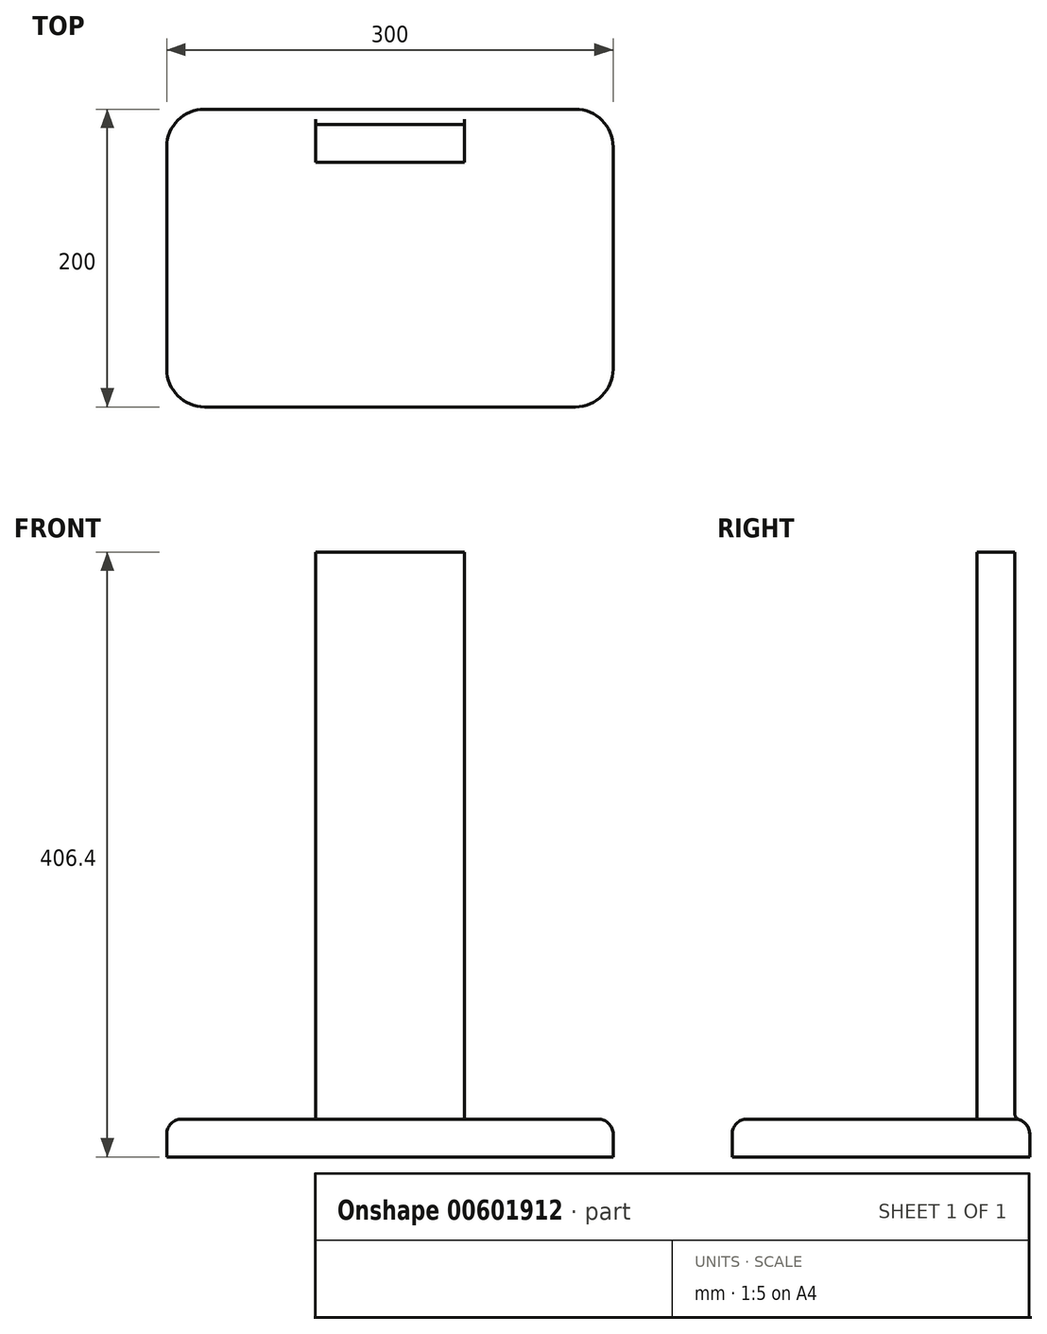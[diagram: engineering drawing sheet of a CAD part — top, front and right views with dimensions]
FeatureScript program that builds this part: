
annotation { "Feature Type Name" : "Feature", "Feature Type Description" : "" }
export const myFeature = defineFeature(function(context is Context, id is Id, definition is map)
    precondition{}
    {
        {
            var Q0;
            Q0=qCreatedBy(makeId("Top.planeOp"),FACE);
            var sketch = newSketch(context, id + "F0", { "sketchPlane" : qUnion([Q0])});
            skLineSegment(sketch, "E0.bottom", {"start": v(-150, 100) * mm, "end": v(150, 100) * mm});
            skLineSegment(sketch, "E0.top", {"start": v(-150, -100) * mm, "end": v(150, -100) * mm});
            skLineSegment(sketch, "E0.left", {"start": v(-150, 100) * mm, "end": v(-150, -100) * mm});
            skLineSegment(sketch, "E0.right", {"start": v(150, 100) * mm, "end": v(150, -100) * mm});
            skSolve(sketch);
        }
        {
            var Q0;
            Q0 = qSketchRegion(id + "F0", true);
            extrude(context, id + "F1", {"entities" : qUnion([Q0]), "depth" : 25.4 * mm, "offsetDistance" : 25.4 * mm});
        }
        {
            var Q0;
            Q0=makeQuery(id+"F1.opExtrude","CAP_EDGE",EDGE,{"disambiguationData":[OSD([sQuery(id+"F0.wireOp",EDGE,"E0.top")])],"isStart":false});
            var Q1;
            Q1=makeQuery(id+"F1.opExtrude","CAP_FACE",FACE,{"disambiguationData":[OSD([sQuery(id+"F0.wireOp",EDGE,"E0.bottom"),sQuery(id+"F0.wireOp",EDGE,"E0.top"),sQuery(id+"F0.wireOp",EDGE,"E0.left"),sQuery(id+"F0.wireOp",EDGE,"E0.right")])],"isStart":false});
            fillet(context, id + "F2", {"entities" : qUnion([Q0, Q1]), "radius" : 10.16 * mm, "tangentPropagation" : true, "allowEdgeOverflow" : false});
        }
        {
            var Q0;
            Q0=makeQuery(id+"F1.opExtrude","SWEPT_EDGE",EDGE,{"disambiguationData":[OSD([sQuery(id+"F0.wireOp",EDGE,"E0.top"),sQuery(id+"F0.wireOp",EDGE,"E0.left")])]});
            var Q1;
            Q1=makeQuery(id+"F1.opExtrude","SWEPT_EDGE",EDGE,{"disambiguationData":[OSD([sQuery(id+"F0.wireOp",EDGE,"E0.top"),sQuery(id+"F0.wireOp",EDGE,"E0.right")])]});
            var Q2;
            Q2=makeQuery(id+"F1.opExtrude","SWEPT_EDGE",EDGE,{"disambiguationData":[OSD([sQuery(id+"F0.wireOp",EDGE,"E0.bottom"),sQuery(id+"F0.wireOp",EDGE,"E0.right")])]});
            var Q3;
            Q3=makeQuery(id+"F1.opExtrude","SWEPT_EDGE",EDGE,{"disambiguationData":[OSD([sQuery(id+"F0.wireOp",EDGE,"E0.bottom"),sQuery(id+"F0.wireOp",EDGE,"E0.left")])]});
            fillet(context, id + "F3", {"entities" : qUnion([Q0, Q1, Q2, Q3]), "radius" : 25.4 * mm, "tangentPropagation" : true, "allowEdgeOverflow" : false});
        }
        {
            var Q0;
            Q0=makeQuery(id+"F1.opExtrude","CAP_FACE",FACE,{"disambiguationData":[OSD([sQuery(id+"F0.wireOp",EDGE,"E0.bottom"),sQuery(id+"F0.wireOp",EDGE,"E0.top"),sQuery(id+"F0.wireOp",EDGE,"E0.left"),sQuery(id+"F0.wireOp",EDGE,"E0.right")])],"isStart":false});
            var sketch = newSketch(context, id + "F4", { "sketchPlane" : qUnion([Q0])});
            skLineSegment(sketch, "E1.bottom", {"start": v(-50, 89.84) * mm, "end": v(50, 89.84) * mm});
            skLineSegment(sketch, "E1.top", {"start": v(-50, 64.44) * mm, "end": v(50, 64.44) * mm});
            skLineSegment(sketch, "E1.left", {"start": v(-50, 89.84) * mm, "end": v(-50, 64.44) * mm});
            skLineSegment(sketch, "E1.right", {"start": v(50, 89.84) * mm, "end": v(50, 64.44) * mm});
            skSolve(sketch);
        }
        {
            var Q0;
            Q0=makeQuery(id+"F4.imprint","IMPRINT",FACE,{"disambiguationData":[TD([[makeQuery(id+"F4.imprint","IMPRINT",EDGE,{"derivedFrom":sQuery(id+"F4.wireOp",EDGE,"E1.bottom")}),1.0]])]});
            extrude(context, id + "F5", {"entities" : qUnion([Q0]), "operationType" : NewBodyOperationType.ADD, "depth" : 381 * mm, "offsetDistance" : 25.4 * mm});
        }
        {
            var Q0;
            Q0=makeQuery(id+"F5.opExtrude","CAP_EDGE",EDGE,{"disambiguationData":[OSD([sQuery(id+"F4.wireOp",EDGE,"E1.top")])],"isStart":true});
            var Q1;
            Q1=makeQuery(id+"F5.opExtrude","CAP_EDGE",EDGE,{"disambiguationData":[OSD([sQuery(id+"F4.wireOp",EDGE,"E1.right")])],"isStart":true});
            var Q2;
            Q2=makeQuery(id+"F5.opExtrude","CAP_EDGE",EDGE,{"disambiguationData":[OSD([sQuery(id+"F4.wireOp",EDGE,"E1.left")])],"isStart":true});
            var Q3;
            {var subQ0=sQuery(id+"F0.wireOp",EDGE,"E0.bottom");Q3=makeQuery(id+"F5.boolean.opBoolean","MERGE",EDGE,{"derivedFrom":[makeQuery(id+"F2.opFillet","BLEND_EDGE",EDGE,{"blendedFrom":[makeQuery(id+"F1.opExtrude","CAP_EDGE",EDGE,{"disambiguationData":[OSD([subQ0])],"isStart":false}),makeQuery(id+"F1.opExtrude","CAP_FACE",FACE,{"disambiguationData":[OSD([subQ0,sQuery(id+"F0.wireOp",EDGE,"E0.top"),sQuery(id+"F0.wireOp",EDGE,"E0.left"),sQuery(id+"F0.wireOp",EDGE,"E0.right")])],"isStart":false})],"blendedInto":[makeQuery(id+"F1.opExtrude","CAP_FACE",FACE,{"disambiguationData":[OSD([subQ0,sQuery(id+"F0.wireOp",EDGE,"E0.top"),sQuery(id+"F0.wireOp",EDGE,"E0.left"),sQuery(id+"F0.wireOp",EDGE,"E0.right")])],"isStart":false})]}),makeQuery(id+"F5.opExtrude","CAP_EDGE",EDGE,{"disambiguationData":[OSD([sQuery(id+"F4.wireOp",EDGE,"E1.bottom")])],"isStart":true})]});}
            fillet(context, id + "F6", {"entities" : qUnion([Q0, Q1, Q2, Q3]), "radius" : 5.08 * mm, "tangentPropagation" : true, "allowEdgeOverflow" : false});
        }
    });
